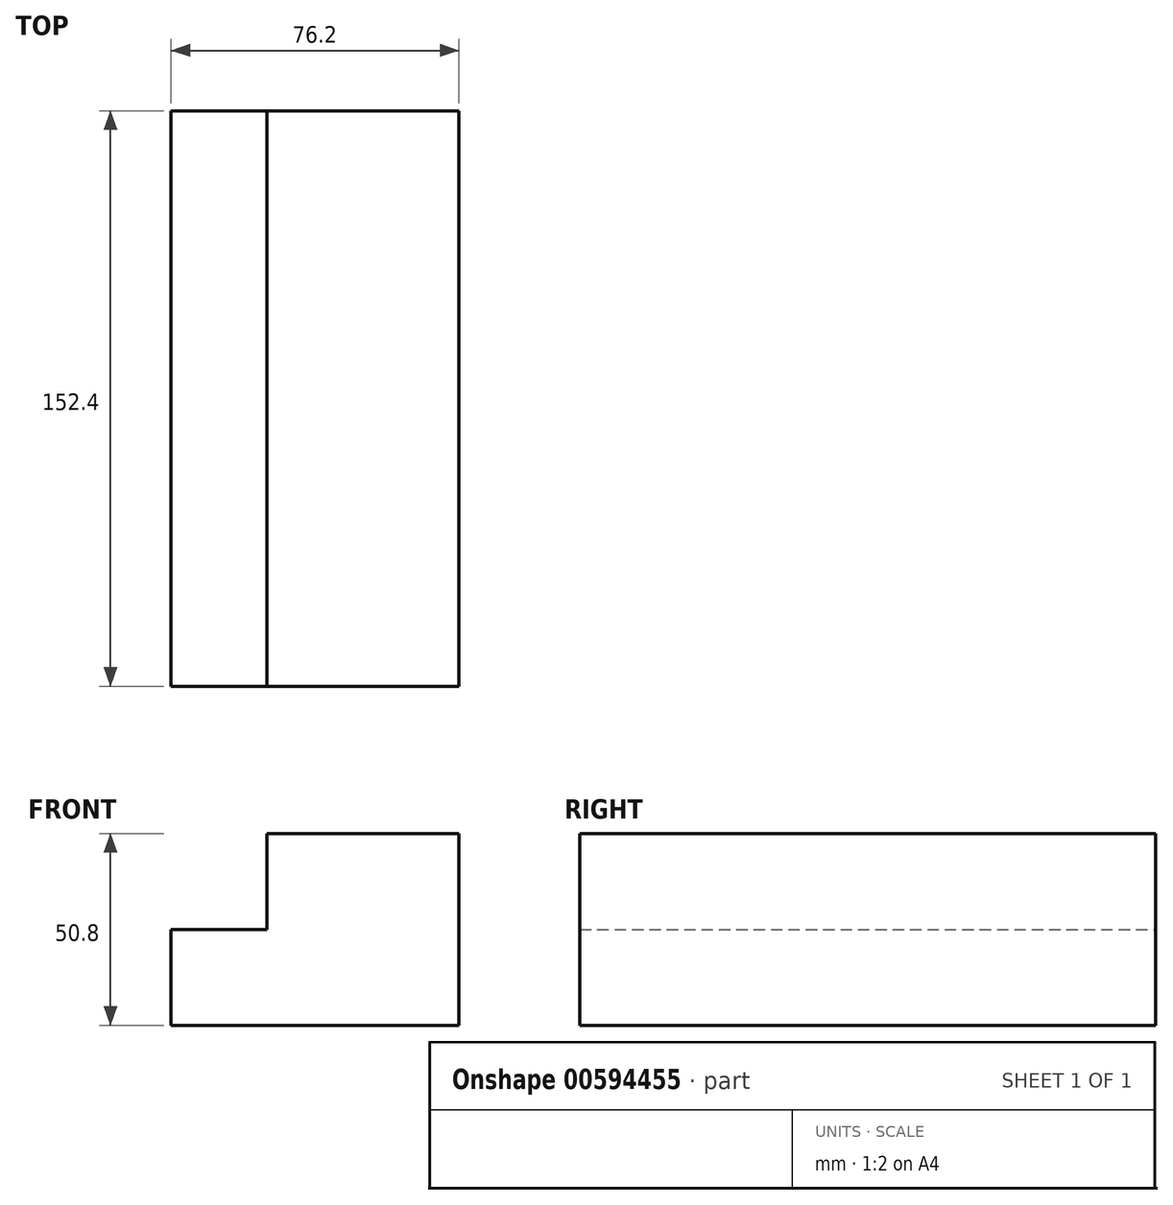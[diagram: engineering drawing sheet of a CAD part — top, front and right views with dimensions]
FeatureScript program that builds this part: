
annotation { "Feature Type Name" : "Feature", "Feature Type Description" : "" }
export const myFeature = defineFeature(function(context is Context, id is Id, definition is map)
    precondition{}
    {
        {
            var Q0;
            Q0=qCreatedBy(makeId("Front.planeOp"),FACE);
            var sketch = newSketch(context, id + "F0", { "sketchPlane" : qUnion([Q0])});
            skLineSegment(sketch, "E0", {"start": v(0, 0) * mm, "end": v(76.2, 0) * mm});
            skLineSegment(sketch, "E1", {"start": v(76.2, 0) * mm, "end": v(76.2, 50.8) * mm});
            skLineSegment(sketch, "E2", {"start": v(76.2, 50.8) * mm, "end": v(25.4, 50.8) * mm});
            skLineSegment(sketch, "E3", {"start": v(25.4, 50.8) * mm, "end": v(25.4, 25.4) * mm});
            skLineSegment(sketch, "E4", {"start": v(25.4, 25.4) * mm, "end": v(0, 25.4) * mm});
            skLineSegment(sketch, "E5", {"start": v(0, 25.4) * mm, "end": v(0, 0) * mm});
            skSolve(sketch);
        }
        {
            var Q0;
            Q0=makeQuery(id+"F0.imprint","IMPRINT",FACE,{"disambiguationData":[TD([[makeQuery(id+"F0.imprint","IMPRINT",EDGE,{"derivedFrom":sQuery(id+"F0.wireOp",EDGE,"E0")}),1.0]])]});
            extrude(context, id + "F1", {"entities" : qUnion([Q0]), "depth" : 152.4 * mm, "offsetDistance" : 25.4 * mm});
        }
    });
